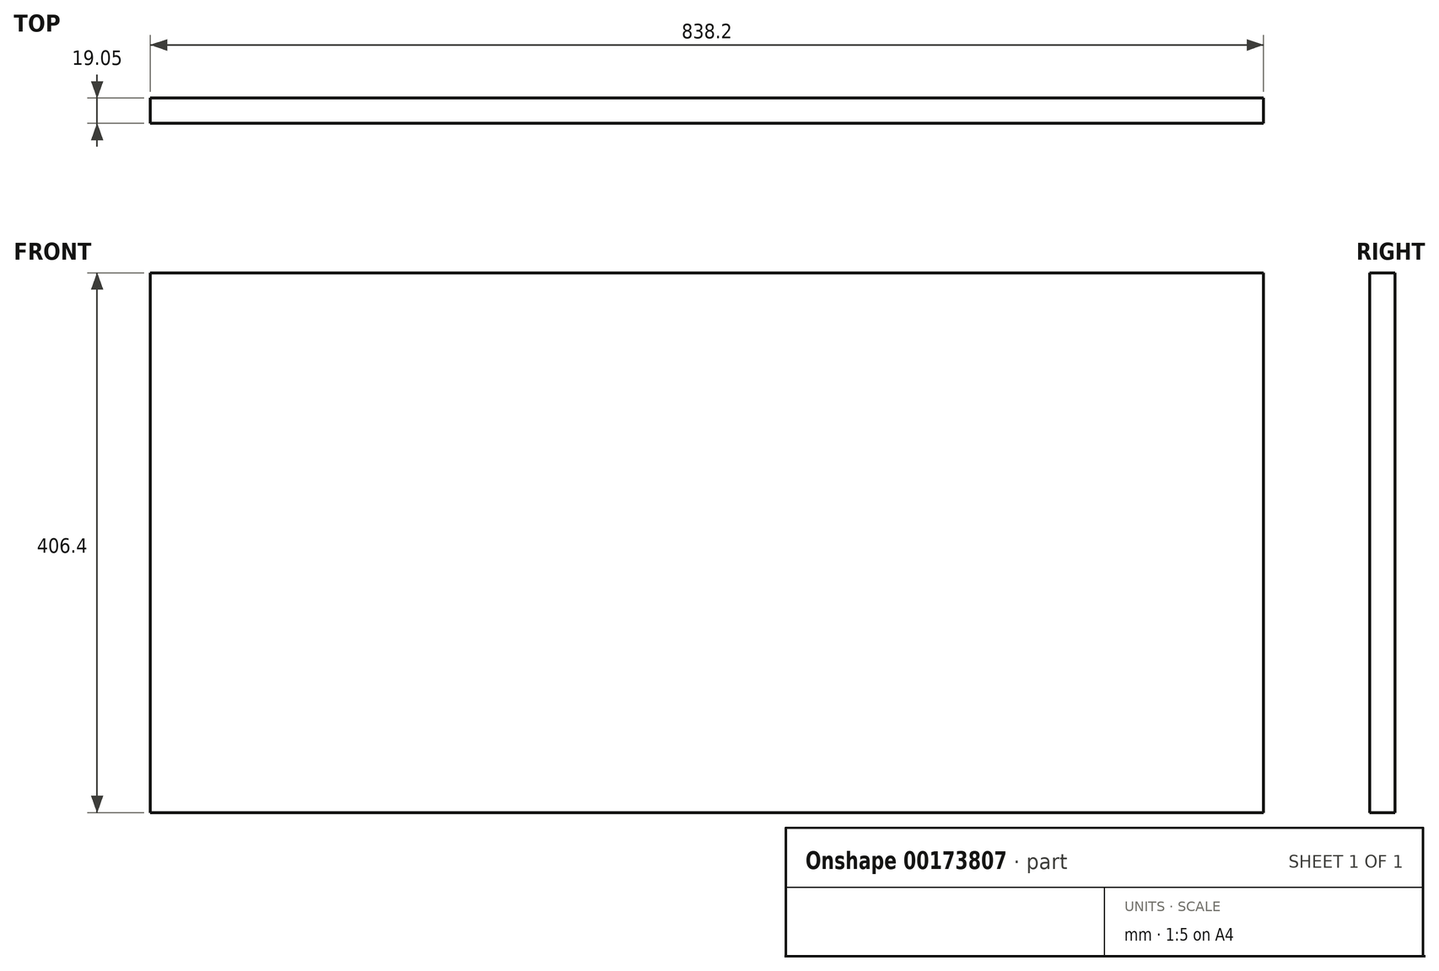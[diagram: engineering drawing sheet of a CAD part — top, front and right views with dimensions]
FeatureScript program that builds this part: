
annotation { "Feature Type Name" : "Feature", "Feature Type Description" : "" }
export const myFeature = defineFeature(function(context is Context, id is Id, definition is map)
    precondition{}
    {
        {
            var Q0;
            Q0=qCreatedBy(makeId("Front.planeOp"),FACE);
            var sketch = newSketch(context, id + "F0", { "sketchPlane" : qUnion([Q0])});
            skLineSegment(sketch, "E0.bottom", {"start": v(419.1, 203.2) * mm, "end": v(-419.1, 203.2) * mm});
            skLineSegment(sketch, "E0.top", {"start": v(419.1, -203.2) * mm, "end": v(-419.1, -203.2) * mm});
            skLineSegment(sketch, "E0.left", {"start": v(419.1, 203.2) * mm, "end": v(419.1, -203.2) * mm});
            skLineSegment(sketch, "E0.right", {"start": v(-419.1, 203.2) * mm, "end": v(-419.1, -203.2) * mm});
            skPoint(sketch, "E0.middle", {"position": v(0, 0) * mm});
            skSolve(sketch);
        }
        {
            var Q0;
            Q0 = qSketchRegion(id + "F0", true);
            extrude(context, id + "F1", {"entities" : qUnion([Q0]), "depth" : 19.05 * mm});
        }
    });
